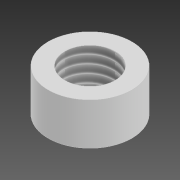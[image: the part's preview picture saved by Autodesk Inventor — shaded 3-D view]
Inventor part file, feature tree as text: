
AUTODESK INVENTOR PART (.ipt)
format: ipt  version: 2020 (Build 240168000, 168)  size: 89,088 bytes
history: native  units: in
note: dims shown in document units (in); Inventor stores cm internally (conversion verified against a paired STEP export)
features: extrude x1, thread x1, sketch x1
ambient origin geometry x8: Origin, YZ Plane, XZ Plane, XY Plane, X Axis, Y Axis, Z Axis, Center Point
bodies: Solid1 (feature_tree)
feature tree (3):
  extrude  "Extrusion1"  Depth=0.1969in
  thread  "Thread4"  [1 undecoded]
  sketch  "Sketch1"  dims[d0=0.3937in d1=0.2362in d2=0.1969in d3=0.0in d10=0.5512in d11=0.0in]
note: 1 required parameter value undecoded (feature->parameter linkage not recoverable at this tier; creation-order binding heuristic only, values carry confidence <= 0.55)
